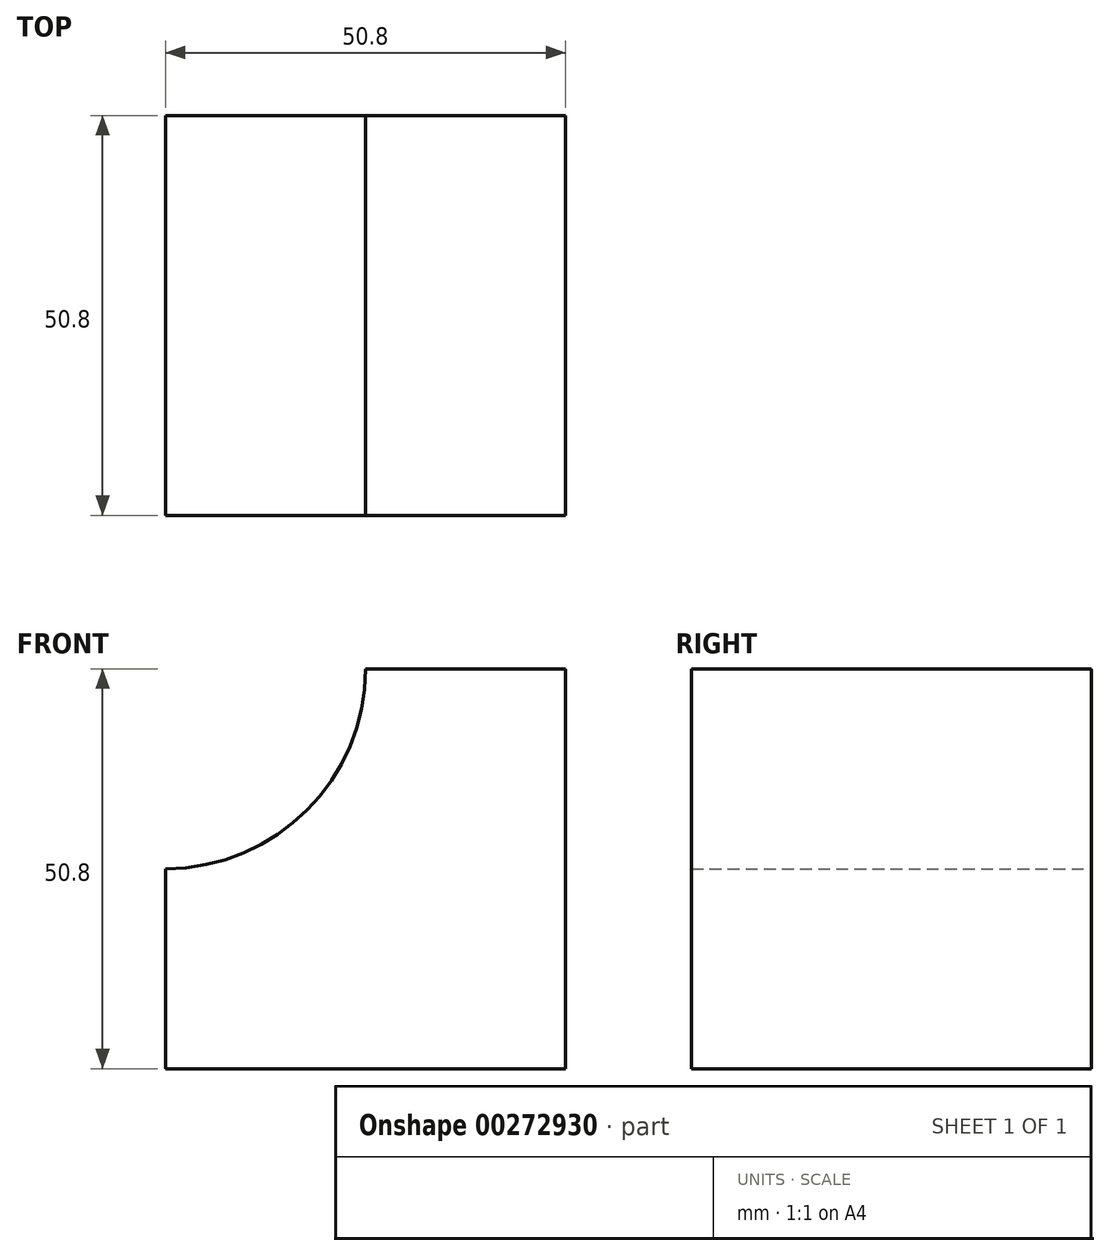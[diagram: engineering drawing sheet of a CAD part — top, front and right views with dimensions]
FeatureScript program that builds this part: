
annotation { "Feature Type Name" : "Feature", "Feature Type Description" : "" }
export const myFeature = defineFeature(function(context is Context, id is Id, definition is map)
    precondition{}
    {
        {
            var Q0;
            Q0=qCreatedBy(makeId("Front.planeOp"),FACE);
            var sketch = newSketch(context, id + "F0", { "sketchPlane" : qUnion([Q0])});
            skLineSegment(sketch, "E0", {"start": v(0, 0) * mm, "end": v(-50.8, 0) * mm});
            skLineSegment(sketch, "E1", {"start": v(0, 0) * mm, "end": v(0, 50.8) * mm});
            skLineSegment(sketch, "E2", {"start": v(0, 50.8) * mm, "end": v(-25.4, 50.8) * mm});
            skLineSegment(sketch, "E3", {"start": v(-50.8, 0) * mm, "end": v(-50.8, 25.4) * mm});
            skArc(sketch, "E4", {"start": v(-50.8, 25.4) * mm, "mid": v(-32.84, 32.84) * mm, "end": v(-25.4, 50.8) * mm});
            skSolve(sketch);
        }
        {
            var Q0;
            Q0 = qSketchRegion(id + "F0", true);
            extrude(context, id + "F1", {"entities" : qUnion([Q0]), "depth" : 50.8 * mm});
        }
    });
